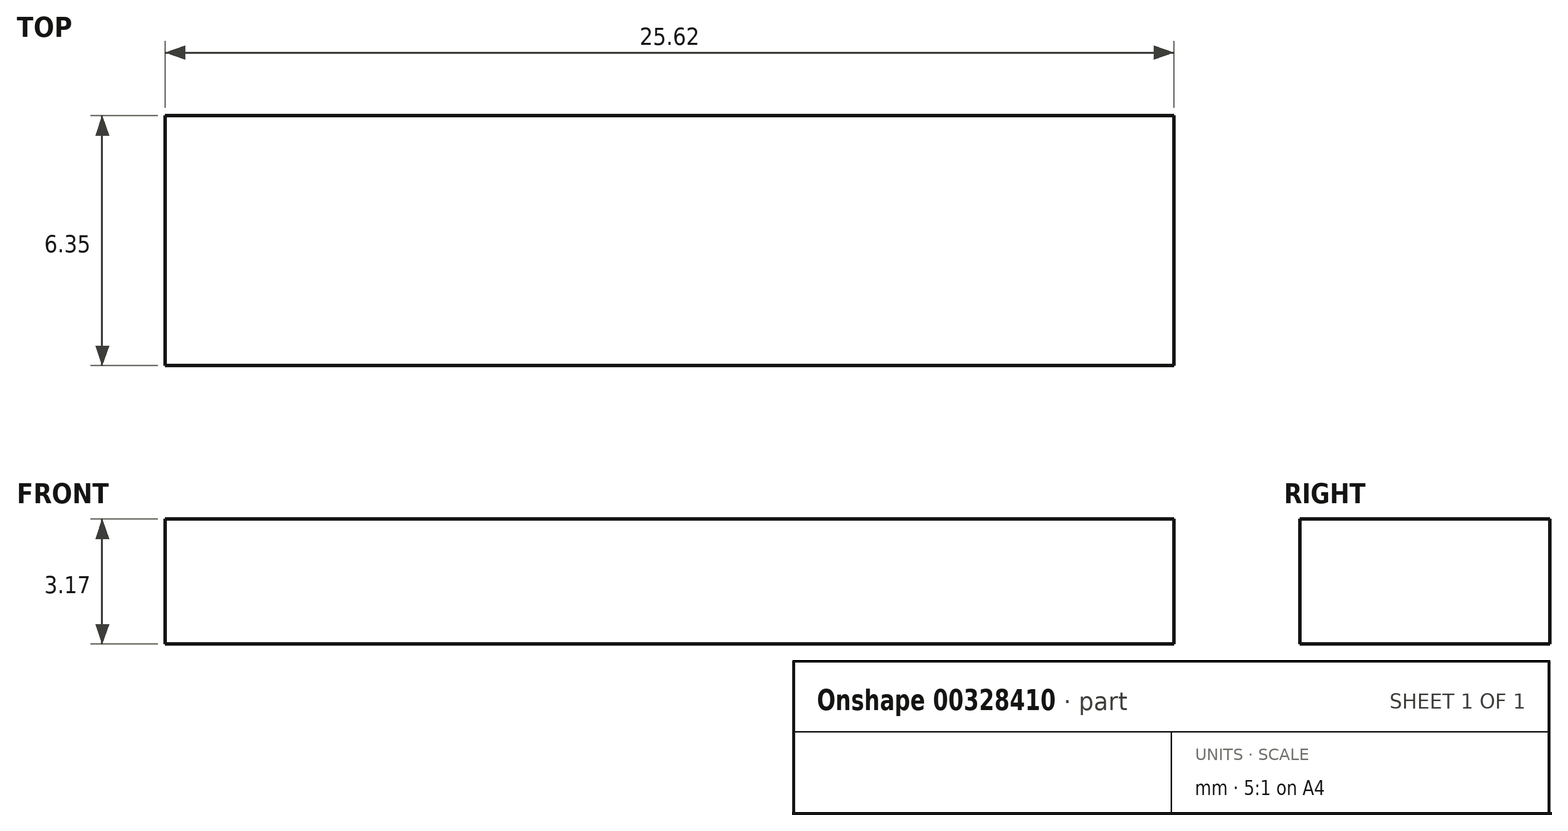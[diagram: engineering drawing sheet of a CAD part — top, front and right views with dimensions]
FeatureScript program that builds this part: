
annotation { "Feature Type Name" : "Feature", "Feature Type Description" : "" }
export const myFeature = defineFeature(function(context is Context, id is Id, definition is map)
    precondition{}
    {
        {
            var Q0;
            Q0=qCreatedBy(makeId("Top.planeOp"),FACE);
            var sketch = newSketch(context, id + "F0", { "sketchPlane" : qUnion([Q0])});
            skLineSegment(sketch, "E0", {"start": v(0, 0) * mm, "end": v(25.62, 0) * mm});
            skLineSegment(sketch, "E1", {"start": v(25.62, 0) * mm, "end": v(25.62, 6.35) * mm});
            skLineSegment(sketch, "E2", {"start": v(25.62, 6.35) * mm, "end": v(0, 6.35) * mm});
            skLineSegment(sketch, "E3", {"start": v(0, 6.35) * mm, "end": v(0, 0) * mm});
            skSolve(sketch);
        }
        {
            var Q0;
            Q0 = qSketchRegion(id + "F0", true);
            extrude(context, id + "F1", {"entities" : qUnion([Q0]), "depth" : 3.17 * mm});
        }
    });
